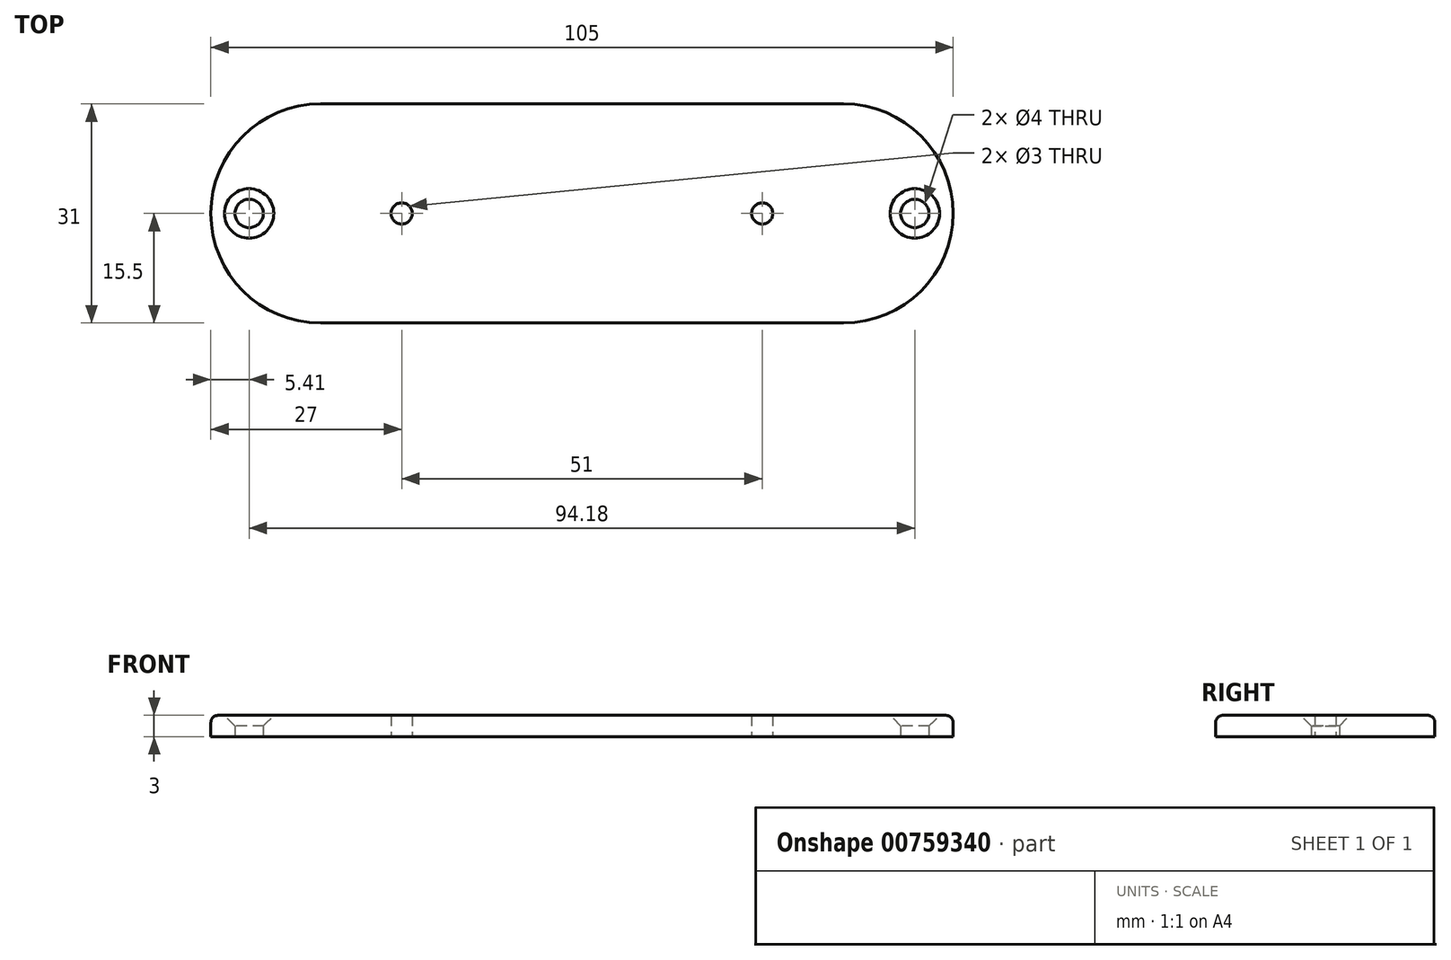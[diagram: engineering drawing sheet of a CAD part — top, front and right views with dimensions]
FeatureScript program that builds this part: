
annotation { "Feature Type Name" : "Feature", "Feature Type Description" : "" }
export const myFeature = defineFeature(function(context is Context, id is Id, definition is map)
    precondition{}
    {
        {
            var Q0;
            Q0=qCreatedBy(makeId("Top.planeOp"),FACE);
            var sketch = newSketch(context, id + "F0", { "sketchPlane" : qUnion([Q0])});
            skLineSegment(sketch, "E0.bottom", {"start": v(-37, 15.5) * mm, "end": v(37, 15.5) * mm});
            skLineSegment(sketch, "E0.top", {"start": v(-37, -15.5) * mm, "end": v(37, -15.5) * mm});
            skPoint(sketch, "E0.middle", {"position": v(0, 0) * mm});
            skArc(sketch, "E1", {"start": v(-37, 15.5) * mm, "mid": v(-52.5, 0) * mm, "end": v(-37, -15.5) * mm});
            skArc(sketch, "E2", {"start": v(37, 15.5) * mm, "mid": v(52.5, 0) * mm, "end": v(37, -15.5) * mm});
            skCircle(sketch, "E3", {"center": v(-47.1, 0) * mm, "radius": 2 * mm});
            skPoint(sketch, "E3.centerSnap0", {"position": v(-52.5, 0) * mm});
            skCircle(sketch, "E4", {"center": v(-25.5, 0) * mm, "radius": 1.5 * mm});
            skCircle(sketch, "E5.MirrorC", {"center": v(25.5, 0) * mm, "radius": 1.5 * mm});
            skCircle(sketch, "E6.MirrorC", {"center": v(47.1, 0) * mm, "radius": 2 * mm});
            skSolve(sketch);
        }
        {
            var Q0;
            Q0=makeQuery(id+"F0.imprint","IMPRINT",FACE,{"disambiguationData":[TD([[makeQuery(id+"F0.imprint","IMPRINT",EDGE,{"derivedFrom":sQuery(id+"F0.wireOp",EDGE,"E0.bottom")}),-1.0]])]});
            extrude(context, id + "F1", {"entities" : qUnion([Q0]), "depth" : 3 * mm, "offsetDistance" : 25 * mm});
        }
        {
            var Q0;
            Q0=makeQuery(id+"F1.opExtrude","CAP_EDGE",EDGE,{"disambiguationData":[OSD([sQuery(id+"F0.wireOp",EDGE,"E2")])],"isStart":false});
            fillet(context, id + "F2", {"entities" : qUnion([Q0]), "radius" : 1 * mm, "tangentPropagation" : true, "allowEdgeOverflow" : false});
        }
        {
            var Q0;
            Q0=makeQuery(id+"F1.opExtrude","CAP_EDGE",EDGE,{"disambiguationData":[OSD([sQuery(id+"F0.wireOp",EDGE,"E3")])],"isStart":false});
            var Q1;
            Q1=makeQuery(id+"F1.opExtrude","CAP_EDGE",EDGE,{"disambiguationData":[OSD([sQuery(id+"F0.wireOp",EDGE,"E6.MirrorC")])],"isStart":false});
            chamfer(context, id + "F3", {"entities" : qUnion([Q0, Q1]), "width" : 1.5 * mm, "tangentPropagation" : true});
        }
    });
